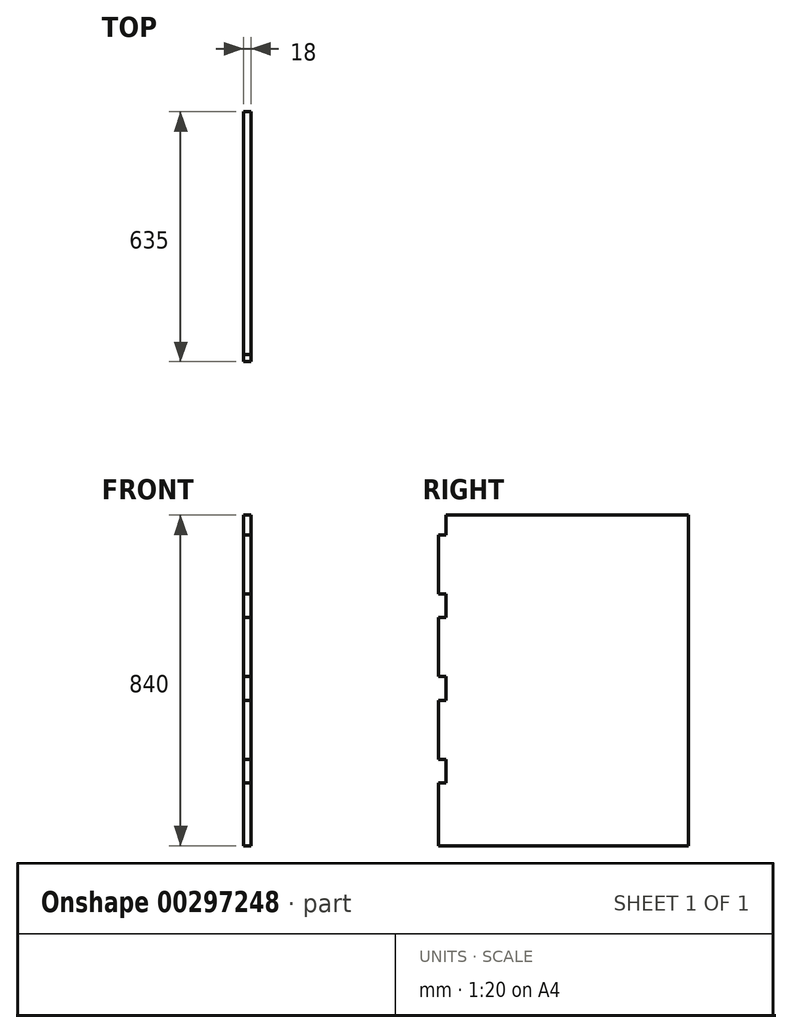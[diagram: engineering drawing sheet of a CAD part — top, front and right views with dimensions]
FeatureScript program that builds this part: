
annotation { "Feature Type Name" : "Feature", "Feature Type Description" : "" }
export const myFeature = defineFeature(function(context is Context, id is Id, definition is map)
    precondition{}
    {
        {
            var Q0;
            Q0=qCreatedBy(makeId("Right.planeOp"),FACE);
            var sketch = newSketch(context, id + "F0", { "sketchPlane" : qUnion([Q0])});
            skLineSegment(sketch, "E0.bottom", {"start": v(317.5, 420) * mm, "end": v(-317.5, 420) * mm});
            skLineSegment(sketch, "E0.top", {"start": v(317.5, -420) * mm, "end": v(-317.5, -420) * mm});
            skLineSegment(sketch, "E0.left", {"start": v(317.5, 420) * mm, "end": v(317.5, -420) * mm});
            skLineSegment(sketch, "E0.right", {"start": v(-317.5, 420) * mm, "end": v(-317.5, -420) * mm});
            skPoint(sketch, "E0.middle", {"position": v(0, 0) * mm});
            skSolve(sketch);
        }
        {
            var Q0;
            Q0=qSketchRegion(id+"F0",true);
            extrude(context, id + "F1", {"entities" : qUnion([Q0]), "depth" : 18 * mm});
        }
        {
            var Q0;
            Q0=makeQuery(id+"F1.opExtrude","CAP_FACE",FACE,{"disambiguationData":[OSD([sQuery(id+"F0.wireOp",EDGE,"E0.bottom"),sQuery(id+"F0.wireOp",EDGE,"E0.top"),sQuery(id+"F0.wireOp",EDGE,"E0.left"),sQuery(id+"F0.wireOp",EDGE,"E0.right")])],"isStart":false});
            var sketch = newSketch(context, id + "F2", { "sketchPlane" : qUnion([Q0])});
            skLineSegment(sketch, "E1.bottom", {"start": v(-317.5, 420) * mm, "end": v(-299.5, 420) * mm});
            skLineSegment(sketch, "E1.top", {"start": v(-317.5, 370) * mm, "end": v(-299.5, 370) * mm});
            skLineSegment(sketch, "E1.left", {"start": v(-317.5, 420) * mm, "end": v(-317.5, 370) * mm});
            skLineSegment(sketch, "E1.right", {"start": v(-299.5, 420) * mm, "end": v(-299.5, 370) * mm});
            skLineSegment(sketch, "E2.bottom", {"start": v(-317.5, 10) * mm, "end": v(-299.5, 10) * mm});
            skLineSegment(sketch, "E2.top", {"start": v(-317.5, -50) * mm, "end": v(-299.5, -50) * mm});
            skLineSegment(sketch, "E2.left", {"start": v(-317.5, 10) * mm, "end": v(-317.5, -50) * mm});
            skLineSegment(sketch, "E2.right", {"start": v(-299.5, 10) * mm, "end": v(-299.5, -50) * mm});
            skLineSegment(sketch, "E3.bottom", {"start": v(-317.5, 160) * mm, "end": v(-299.5, 160) * mm});
            skLineSegment(sketch, "E3.top", {"start": v(-317.5, 220) * mm, "end": v(-299.5, 220) * mm});
            skLineSegment(sketch, "E3.left", {"start": v(-317.5, 160) * mm, "end": v(-317.5, 220) * mm});
            skLineSegment(sketch, "E3.right", {"start": v(-299.5, 160) * mm, "end": v(-299.5, 220) * mm});
            skLineSegment(sketch, "E4.bottom", {"start": v(-317.5, -260) * mm, "end": v(-299.5, -260) * mm});
            skLineSegment(sketch, "E4.top", {"start": v(-317.5, -200) * mm, "end": v(-299.5, -200) * mm});
            skLineSegment(sketch, "E4.left", {"start": v(-317.5, -260) * mm, "end": v(-317.5, -200) * mm});
            skLineSegment(sketch, "E4.right", {"start": v(-299.5, -260) * mm, "end": v(-299.5, -200) * mm});
            skSolve(sketch);
        }
        {
            var Q0;
            Q0=qSketchRegion(id+"F2",true);
            extrude(context, id + "F3", {"entities" : qUnion([Q0]), "operationType" : NewBodyOperationType.REMOVE, "oppositeDirection" : true, "depth" : 18 * mm});
        }
    });
